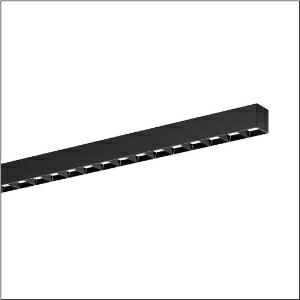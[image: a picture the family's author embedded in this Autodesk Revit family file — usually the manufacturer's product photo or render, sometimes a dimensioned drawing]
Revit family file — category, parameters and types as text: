
# Revit family: silica_r__21_51mx22dc3abb_349a
name_source: partatom
category: Lighting Fixtures
units: mm (PartAtom-declared; Revit-internal decimal feet)

## family parameters
Cut with Voids When Loaded = No
Host = Face
Light Source = No
Part Type = Normal
Room Calculation Point = No
Round Connector Dimension = Use Diameter
Shared = No

## types (1)
- --- (1 x LED, 10800 lm, 69.2 W, 3000K)
    Apparent Load = 69 VA
    CIE Flux Codes = 86 100 100 100 100
    Color Rendering = 80
    Color Temperature = 3000K
    Default Elevation = 1800 mm
    Description = Silica® 21, office luminaire, primary light control with darklight reflector, of PMMA, black, CAT 2 (L<= 3000cd/m²), light emission: direct distribution, primary light characteristic: symmetric, installation type: surface-mounted, LED, rated luminous flux: 10.800lm, luminous efficacy: 156lm/W, light colour: 830, colour temperature: 3000K, with terminal, 3+2-pole, max. 2.5mm², mains connection: 220..240V, AC, 50/60Hz, rated input power: 69.2W, luminaire housing, of aluminium, jet black (RAL 9005), length: 3.004mm, width: 53mm, height: 53mm, protection rating (complete): IP20, insulation class (complete): insulation class I (protective earthing), certification: CE, permissible operating ambient temperature: 0..+35°C, standard: EN 50419, packaging unit: 1 piece
    Height = 0 mm  [stored 0 ft]
    Lamp = 1 x LED
    Lamp Light Flux = 10800 lm
    Lamp Power = 69.2 W
    Lamp count = 1
    Length = 3004 mm
    Luminous efficacy = 156 lm/W
    Manufacturer = Siteco
    ModVariant = No
    Model = 51MX22DC3ABB
    Mounting Place = Ceiling
    Mounting Type = Recessed
    Number of Poles = 1
    OnlyDefault = Yes
    Power Factor = 1
    Product Name = Silica® 21
    Product group = office luminaire | ceiling recessed
    ProductGroupID = 401
    Protection Class = Protection class I
    Protection Degree = IP 20
    RLX_Detail_Level = 1
    RLX_Emergency_Light_Flux = 0 lm
    RLX_Emergency_Type = 0
    RLX_Emergency_Type_DB = No
    RlxData = <blob elided: 64177 chars, md5=4435696b>
    Socket = socket
    Standby Power = 0 W
    System Light Flux = 10800 lm
    System Power = 69 W
    Type Comments = factory setting: luminous flux: 100 % | dim-lin: 254 | 392 mA
    Type Image = l_1313577.jpg
    URL = http://relux.com
    VarID = @adj_074197
    Voltage = 0 V
    Weight = 0.00 kg
    Width = 53 mm

note: [stored X ft] marks values corroborated as IEEE doubles in the binary element streams (Revit-internal decimal feet)

## geometry (parser evidence)
native form markers: Blend x4, Sweep x10
no freeform markers — native parametric forms only
